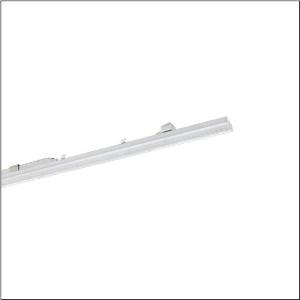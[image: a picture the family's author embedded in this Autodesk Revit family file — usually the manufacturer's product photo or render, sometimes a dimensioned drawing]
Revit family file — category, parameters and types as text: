
# Revit family: tl_l_5wd7a8f0a2c5
name_source: partatom
category: Lighting Fixtures
units: mm (PartAtom-declared; Revit-internal decimal feet)

## family parameters
Cut with Voids When Loaded = No
Host = Face
Light Source = No
Part Type = Normal
Room Calculation Point = No
Round Connector Dimension = Use Diameter
Shared = No

## types (1)
- TL L (1 x LED, 9800 lm, 63.3 W, 4000K)
    Apparent Load = 63 VA
    CIE Flux Codes = 49 84 98 100 100
    Color Rendering = 80
    Color Temperature = 4000K
    Default Elevation = 1800 mm
    Description = TL L, luminaire insert, of sheet steel, galvanised, coil coated, white, length: 1.500mm, width: 66mm, height: 67mm, LED rated luminous flux: 9.800lm, light colour: 840, control gear: 4..20mA, with terminal, 5-pole, mains connection: 230..240V, AC, 50/60Hz, rated input power: 63W, primary optical cover: cover, of PMMA, light emission: direct distribution, protection rating (complete): as luminaire, insulation class (complete): insulation class I (protective earthing), certification: CE, impact resistance: IK06, permissible ambient temperature for indoor applications: -25..+35°C, packaging unit: 1 piece
    Height = 120 mm
    Lamp = 1 x LED
    Lamp Light Flux = 9800 lm
    Lamp Power = 63.3 W
    Lamp count = 1
    Length = 1690 mm
    Luminous efficacy = 155 lm/W
    Manufacturer = Siteco
    ModVariant = No
    Model = 5WD7A8F0A2C5
    Mounting Place = Ceiling
    Mounting Type = Pendant
    Number of Poles = 1
    OnlyDefault = Yes
    Power Factor = 1
    Product Name = TL L
    Product group = luminaire insert
    ProductGroupID = 901
    Protection Class = Protection class I
    Protection Degree = Degree of protection
    RLX_Detail_Level = 1
    RLX_Emergency_Light_Flux = 0 lm
    RLX_Emergency_Type = 0
    RLX_Emergency_Type_DB = No
    RlxData = <blob elided: 14101 chars, md5=0201358c>
    Socket = socket
    Standby Power = 0 W
    System Light Flux = 9800 lm
    System Power = 63 W
    Type Comments = Product without accessories
    Type Image = l_1294382.jpg
    URL = http://relux.com
    VarID = ---
    Voltage = 0 V
    Weight = 0.00 kg
    Width = 208 mm

## geometry (parser evidence)
native form markers: Sweep x12
no freeform markers — native parametric forms only
